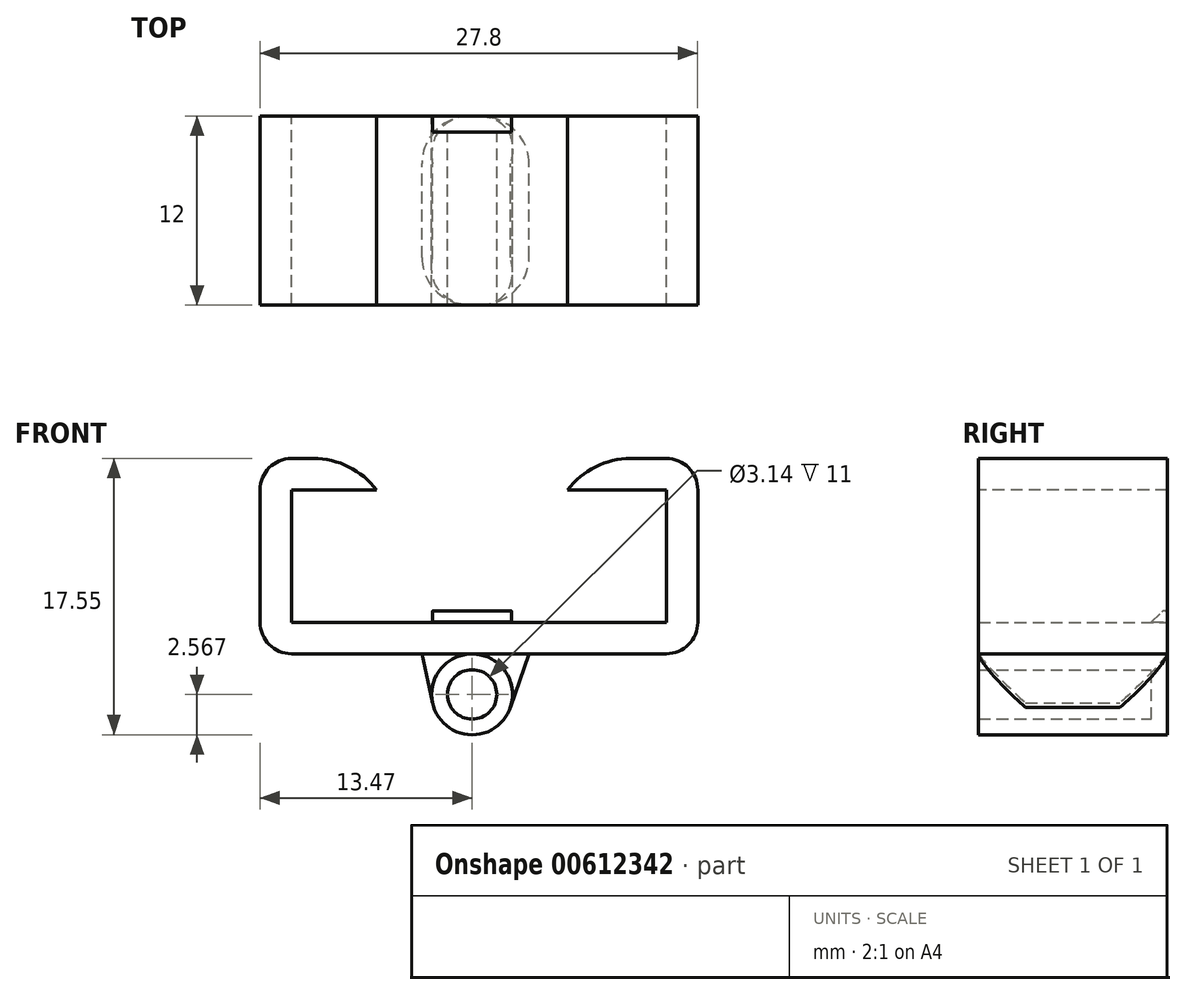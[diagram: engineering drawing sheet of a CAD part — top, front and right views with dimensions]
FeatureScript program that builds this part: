
annotation { "Feature Type Name" : "Feature", "Feature Type Description" : "" }
export const myFeature = defineFeature(function(context is Context, id is Id, definition is map)
    precondition{}
    {
        {
            var Q0;
            Q0=qCreatedBy(makeId("Front.planeOp"),FACE);
            var sketch = newSketch(context, id + "F0", { "sketchPlane" : qUnion([Q0])});
            skLineSegment(sketch, "E0.bottom", {"start": v(-13.47, 5.8) * mm, "end": v(14.33, 5.8) * mm});
            skLineSegment(sketch, "E0.top", {"start": v(-13.47, -6.6) * mm, "end": v(14.33, -6.6) * mm});
            skLineSegment(sketch, "E0.left", {"start": v(-13.47, 5.8) * mm, "end": v(-13.47, -6.6) * mm});
            skLineSegment(sketch, "E0.right", {"start": v(14.33, 5.8) * mm, "end": v(14.33, -6.6) * mm});
            skCircle(sketch, "E1", {"center": v(0, -9.2) * mm, "radius": 2.57 * mm});
            skLineSegment(sketch, "E2", {"start": v(-3.18, -6.6) * mm, "end": v(-2.51, -9.73) * mm});
            skLineSegment(sketch, "E3", {"start": v(3.61, -6.6) * mm, "end": v(2.43, -10.03) * mm});
            skPoint(sketch, "E4.middle", {"position": v(0, 0) * mm});
            skSolve(sketch);
        }
        {
            var Q0;
            Q0=makeQuery(id+"F0.imprint","IMPRINT",FACE,{"disambiguationData":[TD([[makeQuery(id+"F0.imprint","IMPRINT",EDGE,{"derivedFrom":sQuery(id+"F0.wireOp",EDGE,"E0.bottom")}),-1.0]])]});
            extrude(context, id + "F1", {"entities" : qUnion([Q0]), "depth" : 12 * mm, "offsetDistance" : 25 * mm});
        }
        {
            var Q0;
            Q0=makeQuery(id+"F1.opExtrude","CAP_FACE",FACE,{"disambiguationData":[OSD([sQuery(id+"F0.wireOp",EDGE,"E0.bottom"),sQuery(id+"F0.wireOp",EDGE,"E0.top"),sQuery(id+"F0.wireOp",EDGE,"E0.left"),sQuery(id+"F0.wireOp",EDGE,"E0.right")])],"isStart":false});
            shell(context, id + "F2", {"entities" : qUnion([Q0]), "thickness" : 2 * mm});
        }
        {
            var Q0;
            Q0=makeQuery(id+"F2.opShell","OFFSET_FACE",FACE,{"disambiguationData":[OSD([sQuery(id+"F0.wireOp",EDGE,"E0.bottom"),sQuery(id+"F0.wireOp",EDGE,"E0.top"),sQuery(id+"F0.wireOp",EDGE,"E0.left"),sQuery(id+"F0.wireOp",EDGE,"E0.right")])]});
            extrude(context, id + "F3", {"entities" : qUnion([Q0]), "operationType" : NewBodyOperationType.REMOVE, "endBound" : BoundingType.THROUGH_ALL, "oppositeDirection" : true, "depth" : 25 * mm, "offsetDistance" : 25 * mm});
        }
        {
            var Q0;
            Q0=makeQuery(id+"F0.imprint","IMPRINT",FACE,{"disambiguationData":[TD([[makeQuery(id+"F0.imprint","IMPRINT",EDGE,{"derivedFrom":sQuery(id+"F0.wireOp",EDGE,"E1")}),1.0]])]});
            extrude(context, id + "F4", {"entities" : qUnion([Q0]), "depth" : 12 * mm, "offsetDistance" : 25 * mm});
        }
        {
            var Q0;
            Q0=makeQuery(id+"F4.opExtrude","CAP_FACE",FACE,{"disambiguationData":[OSD([sQuery(id+"F0.wireOp",EDGE,"E0.top"),sQuery(id+"F0.wireOp",EDGE,"E1")])],"isStart":false});
            shell(context, id + "F5", {"entities" : qUnion([Q0]), "thickness" : 1 * mm});
        }
        {
            var Q0;
            {var subQ0=sQuery(id+"F0.wireOp",EDGE,"E3");Q0=makeQuery(id+"F0.imprint","IMPRINT",FACE,{"disambiguationData":[TD([[makeQuery(id+"F0.imprint","IMPRINT",EDGE,{"derivedFrom":subQ0}),-1.0]])]});}
            var Q1;
            {var subQ0=sQuery(id+"F0.wireOp",EDGE,"E2");Q1=makeQuery(id+"F0.imprint","IMPRINT",FACE,{"disambiguationData":[TD([[makeQuery(id+"F0.imprint","IMPRINT",EDGE,{"derivedFrom":subQ0}),1.0]])]});}
            extrude(context, id + "F6", {"entities" : qUnion([Q0, Q1]), "depth" : 12 * mm, "offsetDistance" : 25 * mm});
        }
        {
            var Q0;
            Q0=makeQuery(id+"F4.opExtrude","CAP_FACE",FACE,{"disambiguationData":[OSD([sQuery(id+"F0.wireOp",EDGE,"E0.top"),sQuery(id+"F0.wireOp",EDGE,"E1")])],"isStart":true});
            var sketch = newSketch(context, id + "F7", { "sketchPlane" : qUnion([Q0])});
            skLineSegment(sketch, "E5.bottom", {"start": v(2.5, -3.6) * mm, "end": v(-2.5, -3.6) * mm});
            skLineSegment(sketch, "E5.top", {"start": v(2.5, -4.6) * mm, "end": v(-2.5, -4.6) * mm});
            skLineSegment(sketch, "E5.left", {"start": v(2.5, -3.6) * mm, "end": v(2.5, -4.6) * mm});
            skLineSegment(sketch, "E5.right", {"start": v(-2.5, -3.6) * mm, "end": v(-2.5, -4.6) * mm});
            skPoint(sketch, "E6.middle", {"position": v(0, 0) * mm});
            skLineSegment(sketch, "E7.bottom", {"start": v(-6.07, 1.69) * mm, "end": v(6.07, 1.69) * mm});
            skLineSegment(sketch, "E7.top", {"start": v(-6.07, 8.29) * mm, "end": v(6.07, 8.29) * mm});
            skLineSegment(sketch, "E7.left", {"start": v(-6.07, 1.69) * mm, "end": v(-6.07, 8.29) * mm});
            skLineSegment(sketch, "E7.right", {"start": v(6.07, 1.69) * mm, "end": v(6.07, 8.29) * mm});
            skPoint(sketch, "E7.middle", {"position": v(0, 4.99) * mm});
            skSolve(sketch);
        }
        {
            var Q0;
            Q0=makeQuery(id+"F7.imprint","IMPRINT",FACE,{"disambiguationData":[TD([[makeQuery(id+"F7.imprint","IMPRINT",EDGE,{"derivedFrom":sQuery(id+"F7.wireOp",EDGE,"E5.bottom")}),1.0]])]});
            extrude(context, id + "F8", {"entities" : qUnion([Q0]), "operationType" : NewBodyOperationType.ADD, "oppositeDirection" : true, "depth" : 1 * mm, "offsetDistance" : 25 * mm});
        }
        {
            var Q0;
            Q0=makeQuery(id+"F8.opExtrude","CAP_EDGE",EDGE,{"disambiguationData":[OSD([sQuery(id+"F7.wireOp",EDGE,"E5.bottom")])],"isStart":false});
            chamfer(context, id + "F9", {"entities" : qUnion([Q0]), "width" : 1 * mm, "tangentPropagation" : true});
        }
        {
            var Q0;
            {var subQ0=sQuery(id+"F7.wireOp",EDGE,"E5.bottom");Q0=makeQuery(id+"F9.opChamfer","BLEND_EDGE",EDGE,{"blendedFrom":[makeQuery(id+"F8.opExtrude","CAP_EDGE",EDGE,{"disambiguationData":[OSD([subQ0])],"isStart":false}),makeQuery(id+"F8.boolean.opBoolean","MERGE",FACE,{"derivedFrom":[makeQuery(id+"F1.opExtrude","CAP_FACE",FACE,{"disambiguationData":[OSD([sQuery(id+"F0.wireOp",EDGE,"E0.bottom"),sQuery(id+"F0.wireOp",EDGE,"E0.top"),sQuery(id+"F0.wireOp",EDGE,"E0.left"),sQuery(id+"F0.wireOp",EDGE,"E0.right"),sQuery(id+"F0.wireOp",EDGE,"E1")])],"isStart":true}),makeQuery(id+"F8.opExtrude","CAP_FACE",FACE,{"disambiguationData":[OSD([subQ0,sQuery(id+"F7.wireOp",EDGE,"E5.top"),sQuery(id+"F7.wireOp",EDGE,"E5.left"),sQuery(id+"F7.wireOp",EDGE,"E5.right")])],"isStart":true})]})],"blendedInto":[makeQuery(id+"F8.boolean.opBoolean","MERGE",FACE,{"derivedFrom":[makeQuery(id+"F1.opExtrude","CAP_FACE",FACE,{"disambiguationData":[OSD([sQuery(id+"F0.wireOp",EDGE,"E0.bottom"),sQuery(id+"F0.wireOp",EDGE,"E0.top"),sQuery(id+"F0.wireOp",EDGE,"E0.left"),sQuery(id+"F0.wireOp",EDGE,"E0.right"),sQuery(id+"F0.wireOp",EDGE,"E1")])],"isStart":true}),makeQuery(id+"F8.opExtrude","CAP_FACE",FACE,{"disambiguationData":[OSD([subQ0,sQuery(id+"F7.wireOp",EDGE,"E5.top"),sQuery(id+"F7.wireOp",EDGE,"E5.left"),sQuery(id+"F7.wireOp",EDGE,"E5.right")])],"isStart":true})]})]});}
            fillet(context, id + "F10", {"entities" : qUnion([Q0]), "radius" : .2 * mm, "tangentPropagation" : true, "allowEdgeOverflow" : false});
        }
        {
            var Q0;
            Q0=makeQuery(id+"F7.imprint","IMPRINT",FACE,{"disambiguationData":[TD([[makeQuery(id+"F7.imprint","IMPRINT",EDGE,{"derivedFrom":sQuery(id+"F7.wireOp",EDGE,"E6.bottom")}),1.0]])]});
            var Q1;
            Q1=makeQuery(id+"F7.imprint","IMPRINT",FACE,{"disambiguationData":[TD([[makeQuery(id+"F7.imprint","IMPRINT",EDGE,{"derivedFrom":sQuery(id+"F7.wireOp",EDGE,"E7.bottom")}),1.0]])]});
            extrude(context, id + "F11", {"entities" : qUnion([Q0, Q1]), "operationType" : NewBodyOperationType.REMOVE, "endBound" : BoundingType.THROUGH_ALL, "oppositeDirection" : true, "depth" : 25 * mm, "offsetDistance" : 25 * mm});
        }
        {
            var Q0;
            Q0=makeQuery(id+"F1.opExtrude","SWEPT_EDGE",EDGE,{"disambiguationData":[OSD([sQuery(id+"F0.wireOp",EDGE,"E0.bottom"),sQuery(id+"F0.wireOp",EDGE,"E0.left")])]});
            var Q1;
            Q1=makeQuery(id+"F1.opExtrude","SWEPT_EDGE",EDGE,{"disambiguationData":[OSD([sQuery(id+"F0.wireOp",EDGE,"E0.bottom"),sQuery(id+"F0.wireOp",EDGE,"E0.right")])]});
            var Q2;
            Q2=makeQuery(id+"F1.opExtrude","SWEPT_EDGE",EDGE,{"disambiguationData":[OSD([sQuery(id+"F0.wireOp",EDGE,"E0.top"),sQuery(id+"F0.wireOp",EDGE,"E0.right")])]});
            var Q3;
            Q3=makeQuery(id+"F1.opExtrude","SWEPT_EDGE",EDGE,{"disambiguationData":[OSD([sQuery(id+"F0.wireOp",EDGE,"E0.top"),sQuery(id+"F0.wireOp",EDGE,"E0.left")])]});
            fillet(context, id + "F12", {"entities" : qUnion([Q0, Q1, Q2, Q3]), "radius" : 2 * mm, "tangentPropagation" : true, "allowEdgeOverflow" : false});
        }
        {
            var Q0;
            Q0=makeQuery(id+"F6.opExtrude","CAP_EDGE",EDGE,{"disambiguationData":[OSD([sQuery(id+"F0.wireOp",EDGE,"E3")])],"isStart":false});
            var Q1;
            Q1=makeQuery(id+"F6.opExtrude","CAP_EDGE",EDGE,{"disambiguationData":[OSD([sQuery(id+"F0.wireOp",EDGE,"E3")])],"isStart":true});
            var Q2;
            Q2=makeQuery(id+"F6.opExtrude","CAP_EDGE",EDGE,{"disambiguationData":[OSD([sQuery(id+"F0.wireOp",EDGE,"E2")])],"isStart":false});
            var Q3;
            Q3=makeQuery(id+"F6.opExtrude","CAP_EDGE",EDGE,{"disambiguationData":[OSD([sQuery(id+"F0.wireOp",EDGE,"E2")])],"isStart":true});
            fillet(context, id + "F13", {"entities" : qUnion([Q0, Q1, Q2, Q3]), "radius" : 3 * mm, "tangentPropagation" : true, "allowEdgeOverflow" : false});
        }
        {
            var Q0;
            Q0=makeQuery(id+"F11.boolean.opBoolean","INTERSECT",EDGE,{"derivedFrom":[makeQuery(id+"F1.opExtrude","SWEPT_FACE",FACE,{"disambiguationData":[OSD([sQuery(id+"F0.wireOp",EDGE,"E0.bottom")])]}),makeQuery(id+"F11.opExtrude","SWEPT_FACE",FACE,{"disambiguationData":[OSD([sQuery(id+"F7.wireOp",EDGE,"E7.right")])]})]});
            fillet(context, id + "F14", {"entities" : qUnion([Q0]), "radius" : 5 * mm, "tangentPropagation" : true, "allowEdgeOverflow" : false});
        }
        {
            var Q0;
            Q0=makeQuery(id+"F11.boolean.opBoolean","INTERSECT",EDGE,{"derivedFrom":[makeQuery(id+"F1.opExtrude","SWEPT_FACE",FACE,{"disambiguationData":[OSD([sQuery(id+"F0.wireOp",EDGE,"E0.bottom")])]}),makeQuery(id+"F11.opExtrude","SWEPT_FACE",FACE,{"disambiguationData":[OSD([sQuery(id+"F7.wireOp",EDGE,"E7.left")])]})]});
            fillet(context, id + "F15", {"entities" : qUnion([Q0]), "radius" : 5 * mm, "tangentPropagation" : true, "allowEdgeOverflow" : false});
        }
    });
